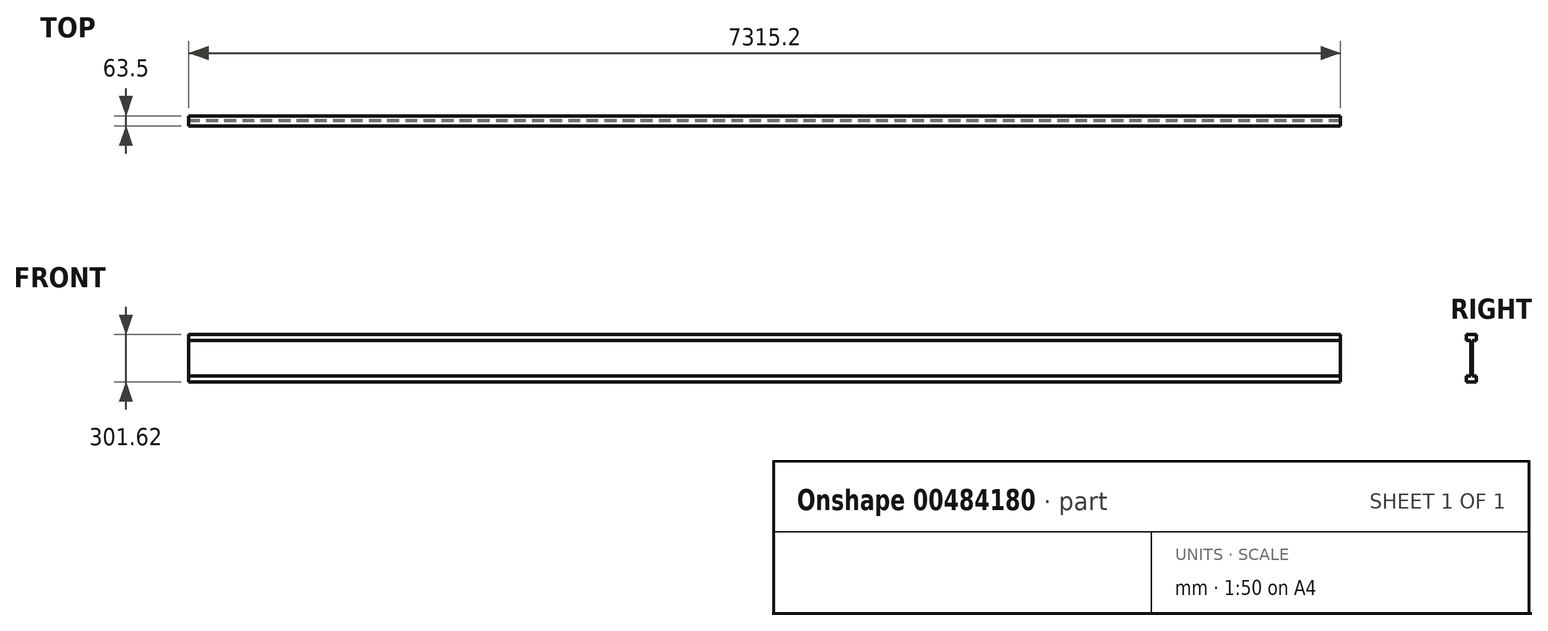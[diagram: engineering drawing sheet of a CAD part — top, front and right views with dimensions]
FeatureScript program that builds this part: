
annotation { "Feature Type Name" : "Feature", "Feature Type Description" : "" }
export const myFeature = defineFeature(function(context is Context, id is Id, definition is map)
    precondition{}
    {
        {
            var Q0;
            Q0=qCreatedBy(makeId("Right.planeOp"),FACE);
            var sketch = newSketch(context, id + "F0", { "sketchPlane" : qUnion([Q0])});
            skLineSegment(sketch, "E0", {"start": v(0, 0) * mm, "end": v(63.5, 0) * mm});
            skLineSegment(sketch, "E1", {"start": v(63.5, 0) * mm, "end": v(63.5, 38.1) * mm});
            skLineSegment(sketch, "E2", {"start": v(63.5, 38.1) * mm, "end": v(36.51, 38.1) * mm});
            skLineSegment(sketch, "E3", {"start": v(36.51, 38.1) * mm, "end": v(36.51, 263.53) * mm});
            skLineSegment(sketch, "E4", {"start": v(36.51, 263.53) * mm, "end": v(63.5, 263.53) * mm});
            skLineSegment(sketch, "E5", {"start": v(63.5, 263.53) * mm, "end": v(63.5, 301.63) * mm});
            skLineSegment(sketch, "E6", {"start": v(63.5, 301.63) * mm, "end": v(0, 301.63) * mm});
            skLineSegment(sketch, "E7", {"start": v(0, 301.63) * mm, "end": v(0, 263.53) * mm});
            skLineSegment(sketch, "E8", {"start": v(0, 263.53) * mm, "end": v(26.99, 263.53) * mm});
            skLineSegment(sketch, "E9", {"start": v(26.99, 263.53) * mm, "end": v(26.99, 38.1) * mm});
            skLineSegment(sketch, "E10", {"start": v(26.99, 38.1) * mm, "end": v(0, 38.1) * mm});
            skLineSegment(sketch, "E11", {"start": v(0, 38.1) * mm, "end": v(0, 0) * mm});
            skSolve(sketch);
        }
        {
            var Q0;
            Q0 = qSketchRegion(id + "F0", true);
            extrude(context, id + "F1", {"entities" : qUnion([Q0]), "depth" : 7315.2 * mm});
        }
    });
